# Revit family: ASH_Contour21_Multiproduct_BIM_GB_S6450;S6452;S6453;S6454;S6455
name_source: partatom
category: Plumbing Fixtures
revit_build: Autodesk Revit MEP 2014 (Build: 20130308_1515(x64)
units: mm (PartAtom-declared; Revit-internal decimal feet)

## types (25) — shared parameters
AccessibilityPerformance = Doc M
Accessories = www.idealspec.co.uk
AreaUnits = millimeters
Assembly Code = C1030200
AssetType = Fixed
BREEAMApproved = No
Brand = Armitage Shanks
ConnectionType = Plumbing
DurationUnit = year
ECA = No
ExpectedLife = 30
Help = www.idealspec.co.uk/contact-us.html
IfcExportAs = IfcValveType
IfcExportType = FAUCET
InstallationInstructions = www.idealspec.co.uk/resources.html
LinearUnits = millimeters
ManufacturerURL = www.idealspec.co.uk
Material = Brass
NBSDescription = Support rails
NBSReference = 45-35-70/360
NominalHeight = 35 mm  [stored 0.114829 ft]
NominalWidth = 100 mm  [stored 0.328084 ft]
Shape = Sculptured
Space = Internal
SpareParts = www.fastpart-spares.co.uk
URL = www.idealspec.co.uk
Uniclass2015Description = Support Rails
Uniclass2015Reference = Pr_40_20_76_84
Uniclass2015Version = Products v1.1
Version = 1
VolumeUnits = Litres
WarrantyDescription = Manufacturers Warranty
WarrantyDurationParts = 5
WarrantyDurationUnit = year
WaterEfficientProduct = No
zero-valued in all types: CWFU, Cost, Default Elevation, HWFU, WFU

## per-type parameters (varying)
| type | BIMObjectName | BarCode | Color | Description | Features | Finish | FinishMtl | Model | ModelNumber | ModelReference | Name | NettWeight | NominalLength | ProductInformation | Size | TMV3 | WRAS |
| S645036 - 300 x 350mm - Blue | ASH_ArmitageShanks_GrabRails_Contour21_S645036 | 5017830384854 | Blue | 300 x 350mm, blue | 300 x 350mm, blue | Blue | ASH_ArmitageShanks_Brassware_Blue_36_Render | S645036 | S645036 | 300 x 350mm, blue | GrabRails_Contour21_S645036_ArmitageShanks | 0.62 Kg | 300 mm | www.idealspec.co.uk/assets/datasheet/S645036 | 35 x 300 x 100 mm | No | No |
| S645236 - Contour21 450 x 350mm - Blue | ASH_ArmitageShanks_GrabRails_Contour21_S645236 | 5017830384861 | Blue | Contour21 450 x 350mm, blue | 450 x 350mm, blue | Blue | ASH_ArmitageShanks_Brassware_Blue_36_Render | S645236 | S645236 | Contour21 450 x 350mm, blue | GrabRails_Contour21_S645236_ArmitageShanks | 0.62 Kg | 400 mm  [stored 1.31234 ft] | www.idealspec.co.uk/assets/datasheet/S645236 | 35 x 400 x 100 mm | Yes | Yes |
| S645336 - Contour21 500 x 350mm - Blue | ASH_ArmitageShanks_GrabRails_Contour21_S645336 | 5017830384878 | Blue | Contour21 500 x 350mm, blue | 500 x 350mm, blue | Blue | ASH_ArmitageShanks_Brassware_Blue_36_Render | S645336 | S645336 | Contour21 500 x 350mm, blue | GrabRails_Contour21_S645336_ArmitageShanks | 0.62 Kg | 500 mm  [stored 1.64042 ft] | www.idealspec.co.uk/assets/datasheet/S645336 | 35 x 500 x 100 mm | Yes | Yes |
| S645436 - Contour21 600 x 350mm - Blue | ASH_ArmitageShanks_GrabRails_Contour21_S645436 | 5017830384885 | Blue | Contour21 600 x 350mm, blue | 600 x 350mm, blue | Blue | ASH_ArmitageShanks_Brassware_Blue_36_Render | S645436 | S645436 | Contour21 600 x 350mm, blue | GrabRails_Contour21_S645436_ArmitageShanks | 0.62 Kg | 600 mm | www.idealspec.co.uk/assets/datasheet/S645436 | 35 x 600 x 100 mm | Yes | Yes |
| S645536 - Contour21 700 x 350mm - Blue | ASH_ArmitageShanks_GrabRails_Contour21_S645536 | 5017830384892 | Blue | Contour21 700 x 350mm, blue | 700 x 350mm, blue | Blue | ASH_ArmitageShanks_Brassware_Blue_36_Render | S645536 | S645536 | Contour21 700 x 350mm, blue | GrabRails_Contour21_S645536_ArmitageShanks | 0.62 Kg | 700 mm  [stored 2.29659 ft] | www.idealspec.co.uk/assets/datasheet/S645536 | 35 x 700 x 100 mm | Yes | Yes |
| S6450AC - 300 x 350mm - White | ASH_ArmitageShanks_GrabRails_Contour21_S6450AC | 5017830383734 | White | 300 x 350mm, white | 300 x 350mm, white | White | ASH_ArmitageShanks_Brassware_White_AC_Render | S6450AC | S6450AC | 300 x 350mm, white | GrabRails_Contour21_S6450AC_ArmitageShanks | 0.62 Kg | 300 mm | www.idealspec.co.uk/assets/datasheet/S6450AC | 35 x 300 x 100 mm | Yes | Yes |
| S6450LJ - 300 x 350mm - Grey | ASH_ArmitageShanks_GrabRails_Contour21_S6450LJ | 5017830384533 | Grey | 300 x 350mm, grey | 300 x 350mm, grey | Grey | ASH_ArmitageShanks_Brassware_Grey_LJ_Render | S6450LJ | S6450LJ | 300 x 350mm, grey | GrabRails_Contour21_S6450LJ_ArmitageShanks | 0.62 Kg | 300 mm | www.idealspec.co.uk/assets/datasheet/S6450LJ | 35 x 300 x 100 mm | Yes | Yes |
| S6450MY - 300 x 350mm - Stainless Steel | ASH_ArmitageShanks_GrabRails_Contour21_S6450MY | 5017830384212 | Steel | 300 x 350mm, stainless steel | 300 x 350mm, stainless steel | Steel | ASH_ArmitageShanks_Brassware_Steel_MY_Render | S6450MY | S6450MY | 300 x 350mm, stainless steel | GrabRails_Contour21_S6450MY_ArmitageShanks | 0.62 Kg | 300 mm | www.idealspec.co.uk/assets/datasheet/S6450MY | 35 x 300 x 100 mm | Yes | Yes |
| S6450RN - 300 x 350mm - Charcoal | ASH_ArmitageShanks_GrabRails_Contour21_S6450RN | 5017830388395 | Charcoal | 300 x 350mm, charcoal | 300 x 350mm, charcoal | Charcoal | ASH_ArmitageShanks_Brassware_Charcoal_RN_Render | S6450RN | S6450RN | 300 x 350mm, charcoal | GrabRails_Contour21_S6450RN_ArmitageShanks | 0.62 Kg | 300 mm | www.idealspec.co.uk/assets/datasheet/S6450RN | 35 x 300 x 100 mm | Yes | Yes |
| S6452AC - Contour21 450 x 350mm - White | ASH_ArmitageShanks_GrabRails_Contour21_S6452AC | 5017830383758 | White | Contour21 450 x 350mm, white | 450 x 350mm, white | White | ASH_ArmitageShanks_Brassware_White_AC_Render | S6452AC | S6452AC | Contour21 450 x 350mm, white | GrabRails_Contour21_S6452AC_ArmitageShanks | 0.62 Kg | 400 mm  [stored 1.31234 ft] | www.idealspec.co.uk/assets/datasheet/S6452AC | 35 x 400 x 100 mm | Yes | Yes |
| S6452LJ - Contour21 450 x 350mm - Grey | ASH_ArmitageShanks_GrabRails_Contour21_S6452LJ | 5017830384540 | Grey | Contour21 450 x 350mm, grey | 450 x 350mm, grey | Grey | ASH_ArmitageShanks_Brassware_Grey_LJ_Render | S6452LJ | S6452LJ | Contour21 450 x 350mm, grey | GrabRails_Contour21_S6452LJ_ArmitageShanks | 0.62 Kg | 400 mm  [stored 1.31234 ft] | www.idealspec.co.uk/assets/datasheet/S6452LJ | 35 x 400 x 100 mm | Yes | Yes |
| S6452MY - Contour21 450 x 350mm - Stainless Steel | ASH_ArmitageShanks_GrabRails_Contour21_S6452MY | 5017830384229 | Steel | Contour21 450 x 350mm, stainless steel | 450 x 350mm, stainless steel | Steel | ASH_ArmitageShanks_Brassware_Steel_MY_Render | S6452MY | S6452MY | Contour21 450 x 350mm, stainless steel | GrabRails_Contour21_S6452MY_ArmitageShanks | 0.62 Kg | 400 mm  [stored 1.31234 ft] | www.idealspec.co.uk/assets/datasheet/S6452MY | 35 x 400 x 100 mm | Yes | Yes |
| S6452RN - Contour21 450 x 350mm - Charcoal | ASH_ArmitageShanks_GrabRails_Contour21_S6452RN | 5017830388401 | Charcoal | Contour21 450 x 350mm, charcoal | 450 x 350mm, charcoal | Charcoal | ASH_ArmitageShanks_Brassware_Charcoal_RN_Render | S6452RN | S6452RN | Contour21 450 x 350mm, charcoal | GrabRails_Contour21_S6452RN_ArmitageShanks | 0.62 Kg | 400 mm  [stored 1.31234 ft] | www.idealspec.co.uk/assets/datasheet/S6452RN | 35 x 400 x 100 mm | Yes | Yes |
| S6453AC - Contour21 500 x 350mm - White | ASH_ArmitageShanks_GrabRails_Contour21_S6453AC | 5017830383765 | White | Contour21 500 x 350mm, white | 500 x 350mm, white | White | ASH_ArmitageShanks_Brassware_White_AC_Render | S6453AC | S6453AC | Contour21 500 x 350mm, white | GrabRails_Contour21_S6453AC_ArmitageShanks | 0.62 Kg | 500 mm  [stored 1.64042 ft] | www.idealspec.co.uk/assets/datasheet/S6453AC | 35 x 500 x 100 mm | Yes | Yes |
| S6453LJ - Contour21 500 x 350mm - Grey | ASH_ArmitageShanks_GrabRails_Contour21_S6453LJ | 5017830384557 | Grey | Contour21 500 x 350mm, grey | 500 x 350mm, grey | Grey | ASH_ArmitageShanks_Brassware_Grey_LJ_Render | S6453LJ | S6453LJ | Contour21 500 x 350mm, grey | GrabRails_Contour21_S6453LJ_ArmitageShanks | 0.62 Kg | 500 mm  [stored 1.64042 ft] | www.idealspec.co.uk/assets/datasheet/S6453LJ | 35 x 500 x 100 mm | Yes | Yes |
| S6453MY - Contour21 500 x 350mm - Stainless Steel | ASH_ArmitageShanks_GrabRails_Contour21_S6453MY | 5017830384236 | Steel | Contour21 500 x 350mm, stainless steel | 500 x 350mm, stainless steel | Steel | ASH_ArmitageShanks_Brassware_Steel_MY_Render | S6453MY | S6453MY | Contour21 500 x 350mm, stainless steel | GrabRails_Contour21_S6453MY_ArmitageShanks | 0.62 Kg | 500 mm  [stored 1.64042 ft] | www.idealspec.co.uk/assets/datasheet/S6453MY | 35 x 500 x 100 mm | Yes | Yes |
| S6453RN - Contour21 500 x 350mm - Charcoal | ASH_ArmitageShanks_GrabRails_Contour21_S6453RN | 5017830388418 | Charcoal | Contour21 500 x 350mm, charcoal | 500 x 350mm, charcoal | Charcoal | ASH_ArmitageShanks_Brassware_Charcoal_RN_Render | S6453RN | S6453RN | Contour21 500 x 350mm, charcoal | GrabRails_Contour21_S6453RN_ArmitageShanks | 0.62 Kg | 500 mm  [stored 1.64042 ft] | www.idealspec.co.uk/assets/datasheet/S6453RN | 35 x 500 x 100 mm | Yes | Yes |
| S6454AC - Contour21 600 x 350mm - White | ASH_ArmitageShanks_GrabRails_Contour21_S6454AC | 5017830383772 | White | Contour21 600 x 350mm, white | 600 x 350mm, white | White | ASH_ArmitageShanks_Brassware_White_AC_Render | S6454AC | S6454AC | Contour21 600 x 350mm, white | GrabRails_Contour21_S6454AC_ArmitageShanks | 2 Kg | 600 mm | www.idealspec.co.uk/assets/datasheet/S6454AC | 35 x 600 x 100 mm | Yes | Yes |
| S6454LJ - Contour21 600 x 350mm - Grey | ASH_ArmitageShanks_GrabRails_Contour21_S6454LJ | 5017830384564 | Grey | Contour21 600 x 350mm, grey | 600 x 350mm, grey | Grey | ASH_ArmitageShanks_Brassware_Grey_LJ_Render | S6454LJ | S6454LJ | Contour21 600 x 350mm, grey | GrabRails_Contour21_S6454LJ_ArmitageShanks | 2 Kg | 600 mm | www.idealspec.co.uk/assets/datasheet/S6454LJ | 35 x 600 x 100 mm | Yes | Yes |
| S6454MY - Contour21 600 x 350mm - Stainless Steel | ASH_ArmitageShanks_GrabRails_Contour21_S6454MY | 5017830384243 | Steel | Contour21 600 x 350mm, stainless steel | 600 x 350mm, stainless steel | Steel | ASH_ArmitageShanks_Brassware_Steel_MY_Render | S6454MY | S6454MY | Contour21 600 x 350mm, stainless steel | GrabRails_Contour21_S6454MY_ArmitageShanks | 2 Kg | 600 mm | www.idealspec.co.uk/assets/datasheet/S6454MY | 35 x 600 x 100 mm | Yes | Yes |
| S6454RN - Contour21 600 x 350mm - Charcoal | ASH_ArmitageShanks_GrabRails_Contour21_S6454RN | 5017830388425 | Charcoal | Contour21 600 x 350mm, charcoal | 600 x 350mm, charcoal | Charcoal | ASH_ArmitageShanks_Brassware_Charcoal_RN_Render | S6454RN | S6454RN | Contour21 600 x 350mm, charcoal | GrabRails_Contour21_S6454RN_ArmitageShanks | 2 Kg | 600 mm | www.idealspec.co.uk/assets/datasheet/S6454RN | 35 x 600 x 100 mm | Yes | Yes |
| S6455AC - Contour21 700 x 350mm - White | ASH_ArmitageShanks_GrabRails_Contour21_S6455AC | 5017830383789 | White | Contour21 700 x 350mm, white | 700 x 350mm, white | White | ASH_ArmitageShanks_Brassware_White_AC_Render | S6455AC | S6455AC | Contour21 700 x 350mm, white | GrabRails_Contour21_S6455AC_ArmitageShanks | 0.62 Kg | 700 mm  [stored 2.29659 ft] | www.idealspec.co.uk/assets/datasheet/S6455AC | 35 x 700 x 100 mm | Yes | Yes |
| S6455LJ - Contour21 700 x 350mm - Grey | ASH_ArmitageShanks_GrabRails_Contour21_S6455LJ | 5017830384571 | Grey | Contour21 700 x 350mm, grey | 700 x 350mm, grey | Grey | ASH_ArmitageShanks_Brassware_Grey_LJ_Render | S6455LJ | S6455LJ | Contour21 700 x 350mm, grey | GrabRails_Contour21_S6455LJ_ArmitageShanks | 0.62 Kg | 700 mm  [stored 2.29659 ft] | www.idealspec.co.uk/assets/datasheet/S6455LJ | 35 x 700 x 100 mm | Yes | Yes |
| S6455MY - Contour21 700 x 350mm - Stainless Steel | ASH_ArmitageShanks_GrabRails_Contour21_S6455MY | 5017830384250 | Steel | Contour21 700 x 350mm, stainless steel | 700 x 350mm, stainless steel | Steel | ASH_ArmitageShanks_Brassware_Steel_MY_Render | S6455MY | S6455MY | Contour21 700 x 350mm, stainless steel | GrabRails_Contour21_S6455MY_ArmitageShanks | 0.62 Kg | 700 mm  [stored 2.29659 ft] | www.idealspec.co.uk/assets/datasheet/S6455MY | 35 x 700 x 100 mm | Yes | Yes |
| S6455RN - Contour21 700 x 350mm - Charcoal | ASH_ArmitageShanks_GrabRails_Contour21_S6455RN | 5017830388432 | Charcoal | Contour21 700 x 350mm, charcoal | 700 x 350mm, charcoal | Charcoal | ASH_ArmitageShanks_Brassware_Charcoal_RN_Render | S6455RN | S6455RN | Contour21 700 x 350mm, charcoal | GrabRails_Contour21_S6455RN_ArmitageShanks | 0.62 Kg | 700 mm  [stored 2.29659 ft] | www.idealspec.co.uk/assets/datasheet/S6455RN | 35 x 700 x 100 mm | Yes | Yes |

note: [stored X ft] marks values corroborated as IEEE doubles in the binary element streams (Revit-internal decimal feet)

## geometry (parser evidence)
native form markers: Sweep x3
no freeform markers — native parametric forms only
